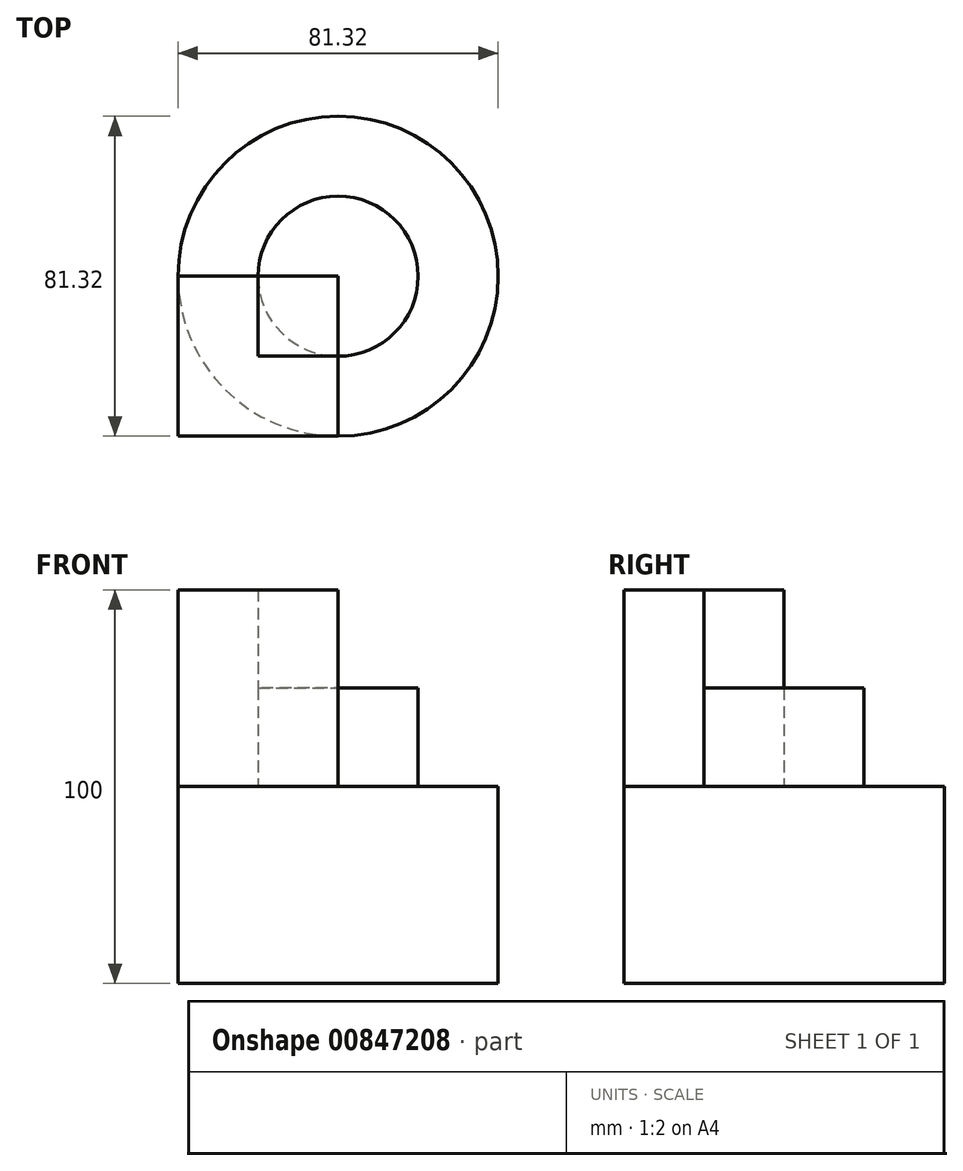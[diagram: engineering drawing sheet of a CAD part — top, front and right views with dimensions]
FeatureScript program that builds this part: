
annotation { "Feature Type Name" : "Feature", "Feature Type Description" : "" }
export const myFeature = defineFeature(function(context is Context, id is Id, definition is map)
    precondition{}
    {
        {
            var Q0;
            Q0=qCreatedBy(makeId("Top.planeOp"),FACE);
            var sketch = newSketch(context, id + "F0", { "sketchPlane" : qUnion([Q0])});
            skCircle(sketch, "E0", {"center": v(0, 0) * mm, "radius": 20.33 * mm});
            skSolve(sketch);
        }
        {
            var Q0;
            Q0 = qSketchRegion(id + "F0", true);
            extrude(context, id + "F1", {"entities" : qUnion([Q0]), "depth" : 25 * mm, "offsetDistance" : 25 * mm});
        }
        {
            var Q0;
            Q0=makeQuery(id+"F1.opExtrude","CAP_FACE",FACE,{"disambiguationData":[OSD([sQuery(id+"F0.wireOp",EDGE,"E0")])],"isStart":false});
            var sketch = newSketch(context, id + "F2", { "sketchPlane" : qUnion([Q0])});
            skLineSegment(sketch, "E1.bottom", {"start": v(-20.33, 0) * mm, "end": v(0, 0) * mm});
            skLineSegment(sketch, "E1.top", {"start": v(-20.33, -20.33) * mm, "end": v(0, -20.33) * mm});
            skLineSegment(sketch, "E1.left", {"start": v(-20.33, 0) * mm, "end": v(-20.33, -20.33) * mm});
            skLineSegment(sketch, "E1.right", {"start": v(0, 0) * mm, "end": v(0, -20.33) * mm});
            skSolve(sketch);
        }
        {
            var Q0;
            Q0 = qSketchRegion(id + "F2", true);
            extrude(context, id + "F3", {"entities" : qUnion([Q0]), "operationType" : NewBodyOperationType.ADD, "depth" : 25 * mm, "offsetDistance" : 25 * mm});
        }
        {
            var Q0;
            Q0=makeQuery(id+"F1.opExtrude","SWEPT_BODY",BODY,{"disambiguationData":[OSD([sQuery(id+"F0.wireOp",EDGE,"E0")])]});
            var Q1;
            Q1=makeQuery(id+"F3.opExtrude","CAP_VERTEX",VERTEX,{"disambiguationData":[OSD([sQuery(id+"F2.wireOp",EDGE,"E1.bottom"),sQuery(id+"F2.wireOp",EDGE,"E1.right")])],"isStart":false});
            transform(context, id + "F4", {"entities" : qUnion([Q0]), "transformType" : TransformType.SCALE_UNIFORMLY, "scale" : 2, "scalePoint" : qUnion([Q1]), "makeCopy" : true});
        }
    });
